# Revit family: Partition-5_Panels_High-Skyfold_Classic_Compact-8-1_to_10-0_FC_2450_to_3050
name_source: partatom
category: Generic Models
units: mm (PartAtom-declared; Revit-internal decimal feet)

## family parameters
Always vertical = Yes
Can host rebar = No
Cut with Voids When Loaded = No
Host = Ceiling
Maintain Annotation Orientation = No
Part Type = Normal
Room Calculation Point = No
Round Connector Dimension = Use Diameter
Shared = No

## types (5) — shared parameters
Default Elevation = 0' - 0"
Description = Custom Powerlift Partitions
Distance From Acoustic Barrier = 0' - 2"
Manufacturer = Skyfold
Model = Compact Drive System
URL = http://www.skyfold.com
Wall Thickness = 0' - 11 3/4"

## per-type parameters (varying)
| type | Acoustic Barrier"C" | Beam Height"B" | Finished Ceiling"A" | Panel Height"F" | Pocket Depth"D" | Pocket Width"E" | Total Panel Height |
| 8'-  1" | 9' - 8" | 10' - 8 1/2" | 8' - 1" | 1' - 10" | 1' - 8" | 4' - 6 3/4" | 9' - 4" |
| 9' - 0" | 10' - 7 1/4" | 11' - 7 3/4" | 9' - 0" | 2' - 0 1/4" | 1' - 8 1/4" | 4' - 11 1/4" | 10' - 3 1/4" |
| 8' - 6" | 10' - 1" | 11' - 1 1/2" | 8' - 6" | 1' - 11" | 1' - 8" | 4' - 8 3/4" | 9' - 9" |
| 9' - 6" | 11' - 1 1/2" | 12' - 2" | 9' - 6" | 2' - 1 1/2" | 1' - 8 1/2" | 5' - 1 3/4" | 10' - 9 1/2" |
| 10' - 0" | 11' - 6 1/2" | 12' - 7" | 10' - 0" | 2' - 2 1/2" | 1' - 7 1/2" | 5' - 3 3/4" | 11' - 2 1/2" |

## geometry (parser evidence)
native form markers: Sweep x24
no freeform markers — native parametric forms only
